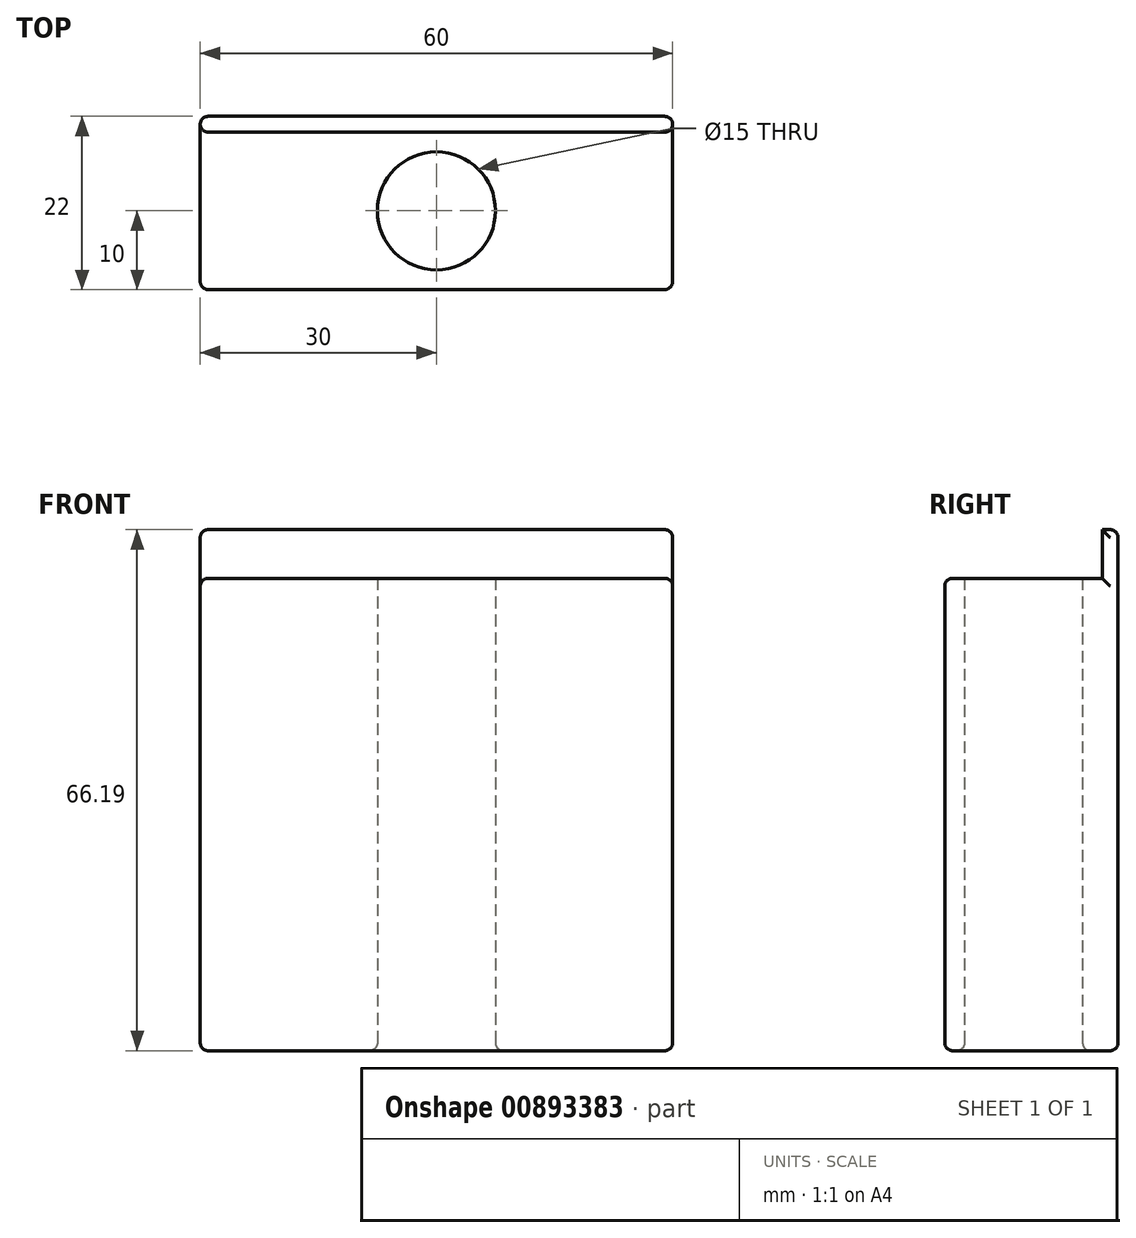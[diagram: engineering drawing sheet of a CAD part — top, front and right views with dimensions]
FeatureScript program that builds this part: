
annotation { "Feature Type Name" : "Feature", "Feature Type Description" : "" }
export const myFeature = defineFeature(function(context is Context, id is Id, definition is map)
    precondition{}
    {
        {
            var Q0;
            Q0=qCreatedBy(makeId("Top.planeOp"),FACE);
            var sketch = newSketch(context, id + "F0", { "sketchPlane" : qUnion([Q0])});
            skLineSegment(sketch, "E0.bottom", {"start": v(0, 0) * mm, "end": v(-60, 0) * mm});
            skLineSegment(sketch, "E0.top", {"start": v(0, 20) * mm, "end": v(-60, 20) * mm});
            skLineSegment(sketch, "E0.left", {"start": v(0, 0) * mm, "end": v(0, 20) * mm});
            skLineSegment(sketch, "E0.right", {"start": v(-60, 0) * mm, "end": v(-60, 20) * mm});
            skLineSegment(sketch, "E1", {"start": v(-30, 20) * mm, "end": v(-30, 0) * mm});
            skLineSegment(sketch, "E2", {"start": v(-60, 10) * mm, "end": v(0, 10) * mm});
            skCircle(sketch, "E3", {"center": v(-30, 10) * mm, "radius": 7.5 * mm});
            skSolve(sketch);
        }
        {
            var Q0;
            {var subQ1=sQuery(id+"F0.wireOp",EDGE,"E0.right");var subQ5=sQuery(id+"F0.wireOp",EDGE,"E0.top");var subQ6=makeQuery(id+"F0.imprint","INTERSECT",VERTEX,{"derivedFrom":[subQ5,subQ1]});Q0=makeQuery(id+"F0.imprint","IMPRINT",FACE,{"disambiguationData":[TD([[makeQuery(id+"F0.imprint","IMPRINT",EDGE,{"disambiguationData":[TD([[subQ6,1.0]])],"derivedFrom":subQ5}),1.0]])]});}
            var Q1;
            {var subQ1=sQuery(id+"F0.wireOp",EDGE,"E0.top");var subQ6=sQuery(id+"F0.wireOp",EDGE,"E0.left");var subQ9=makeQuery(id+"F0.imprint","INTERSECT",VERTEX,{"derivedFrom":[subQ1,subQ6]});Q1=makeQuery(id+"F0.imprint","IMPRINT",FACE,{"disambiguationData":[TD([[makeQuery(id+"F0.imprint","IMPRINT",EDGE,{"disambiguationData":[TD([[subQ9,-1.0]])],"derivedFrom":subQ1}),1.0]])]});}
            var Q2;
            {var subQ1=sQuery(id+"F0.wireOp",EDGE,"E0.bottom");var subQ5=sQuery(id+"F0.wireOp",EDGE,"E0.left");var subQ6=makeQuery(id+"F0.imprint","INTERSECT",VERTEX,{"derivedFrom":[subQ1,subQ5]});Q2=makeQuery(id+"F0.imprint","IMPRINT",FACE,{"disambiguationData":[TD([[makeQuery(id+"F0.imprint","IMPRINT",EDGE,{"disambiguationData":[TD([[subQ6,-1.0]])],"derivedFrom":subQ1}),-1.0]])]});}
            var Q3;
            {var subQ1=sQuery(id+"F0.wireOp",EDGE,"E0.right");var subQ5=sQuery(id+"F0.wireOp",EDGE,"E0.bottom");var subQ6=makeQuery(id+"F0.imprint","INTERSECT",VERTEX,{"derivedFrom":[subQ5,subQ1]});Q3=makeQuery(id+"F0.imprint","IMPRINT",FACE,{"disambiguationData":[TD([[makeQuery(id+"F0.imprint","IMPRINT",EDGE,{"disambiguationData":[TD([[subQ6,1.0]])],"derivedFrom":subQ5}),-1.0]])]});}
            extrude(context, id + "F1", {"entities" : qUnion([Q0, Q1, Q2, Q3]), "depth" : 60 * mm, "offsetDistance" : 25 * mm});
        }
        {
            var Q0;
            Q0=makeQuery(id+"F1.opExtrude","SWEPT_FACE",FACE,{"disambiguationData":[OSD([sQuery(id+"F0.wireOp",EDGE,"E0.right")])]});
            var sketch = newSketch(context, id + "F2", { "sketchPlane" : qUnion([Q0])});
            skLineSegment(sketch, "E4.bottom", {"start": v(-20, 0) * mm, "end": v(-22, 0) * mm});
            skLineSegment(sketch, "E4.top", {"start": v(-20, 66.19) * mm, "end": v(-22, 66.19) * mm});
            skLineSegment(sketch, "E4.left", {"start": v(-20, 0) * mm, "end": v(-20, 66.19) * mm});
            skLineSegment(sketch, "E4.right", {"start": v(-22, 0) * mm, "end": v(-22, 66.19) * mm});
            skSolve(sketch);
        }
        {
            var Q0;
            {var subQ4=sQuery(id+"F2.wireOp",EDGE,"E4.bottom");Q0=makeQuery(id+"F2.imprint","IMPRINT",FACE,{"disambiguationData":[TD([[makeQuery(id+"F2.imprint","IMPRINT",EDGE,{"derivedFrom":subQ4}),-1.0]])]});}
            extrude(context, id + "F3", {"entities" : qUnion([Q0]), "operationType" : NewBodyOperationType.ADD, "oppositeDirection" : true, "depth" : 60 * mm, "offsetDistance" : 25 * mm});
        }
        {
            var Q0;
            Q0=makeQuery(id+"F3.opExtrude","CAP_EDGE",EDGE,{"disambiguationData":[OSD([sQuery(id+"F2.wireOp",EDGE,"E4.right")])],"isStart":false});
            var Q1;
            Q1=makeQuery(id+"F3.boolean.opBoolean","MERGE",FACE,{"derivedFrom":[makeQuery(id+"F1.opExtrude","SWEPT_FACE",FACE,{"disambiguationData":[OSD([sQuery(id+"F0.wireOp",EDGE,"E0.right")])]}),makeQuery(id+"F3.opExtrude","CAP_FACE",FACE,{"disambiguationData":[OSD([sQuery(id+"F2.wireOp",EDGE,"E4.bottom"),sQuery(id+"F2.wireOp",EDGE,"E4.top"),sQuery(id+"F2.wireOp",EDGE,"E4.left"),sQuery(id+"F2.wireOp",EDGE,"E4.right")])],"isStart":true})]});
            var Q2;
            Q2=makeQuery(id+"F3.opExtrude","SWEPT_FACE",FACE,{"disambiguationData":[OSD([sQuery(id+"F2.wireOp",EDGE,"E4.right")])]});
            var Q3;
            Q3=makeQuery(id+"F3.boolean.opBoolean","MERGE",FACE,{"derivedFrom":[makeQuery(id+"F1.opExtrude","CAP_FACE",FACE,{"disambiguationData":[OSD([sQuery(id+"F0.wireOp",EDGE,"E0.bottom"),sQuery(id+"F0.wireOp",EDGE,"E0.top"),sQuery(id+"F0.wireOp",EDGE,"E0.left"),sQuery(id+"F0.wireOp",EDGE,"E0.right"),sQuery(id+"F0.wireOp",EDGE,"E3")])],"isStart":true}),makeQuery(id+"F3.opExtrude","SWEPT_FACE",FACE,{"disambiguationData":[OSD([sQuery(id+"F2.wireOp",EDGE,"E4.bottom")])]})]});
            var Q4;
            Q4=makeQuery(id+"F3.boolean.opBoolean","MERGE",FACE,{"derivedFrom":[makeQuery(id+"F1.opExtrude","SWEPT_FACE",FACE,{"disambiguationData":[OSD([sQuery(id+"F0.wireOp",EDGE,"E0.left")])]}),makeQuery(id+"F3.opExtrude","CAP_FACE",FACE,{"disambiguationData":[OSD([sQuery(id+"F2.wireOp",EDGE,"E4.bottom"),sQuery(id+"F2.wireOp",EDGE,"E4.top"),sQuery(id+"F2.wireOp",EDGE,"E4.left"),sQuery(id+"F2.wireOp",EDGE,"E4.right")])],"isStart":false})]});
            var Q5;
            Q5=makeQuery(id+"F1.opExtrude","SWEPT_FACE",FACE,{"disambiguationData":[OSD([sQuery(id+"F0.wireOp",EDGE,"E0.bottom")])]});
            fillet(context, id + "F4", {"entities" : qUnion([Q0, Q1, Q2, Q3, Q4, Q5]), "radius" : 1 * mm, "tangentPropagation" : true, "allowEdgeOverflow" : false});
        }
        {
            var Q0;
            Q0=makeQuery(id+"F3.opExtrude","SWEPT_FACE",FACE,{"disambiguationData":[OSD([sQuery(id+"F2.wireOp",EDGE,"E4.left")])]});
            var sketch = newSketch(context, id + "F5", { "sketchPlane" : qUnion([Q0])});
            skLineSegment(sketch, "E5", {"start": v(-30, 66.19) * mm, "end": v(-30, 60) * mm});
            skSolve(sketch);
        }
        {
            var Q0;
            Q0=sQuery(id+"F5.wireOp",EDGE,"E5");
            extrude(context, id + "F6", {"bodyType" : ToolBodyType.SURFACE, "surfaceEntities" : qUnion([Q0]), "endBound" : BoundingType.SYMMETRIC, "depth" : 6.6 * mm, "offsetDistance" : 25 * mm});
        }
    });
